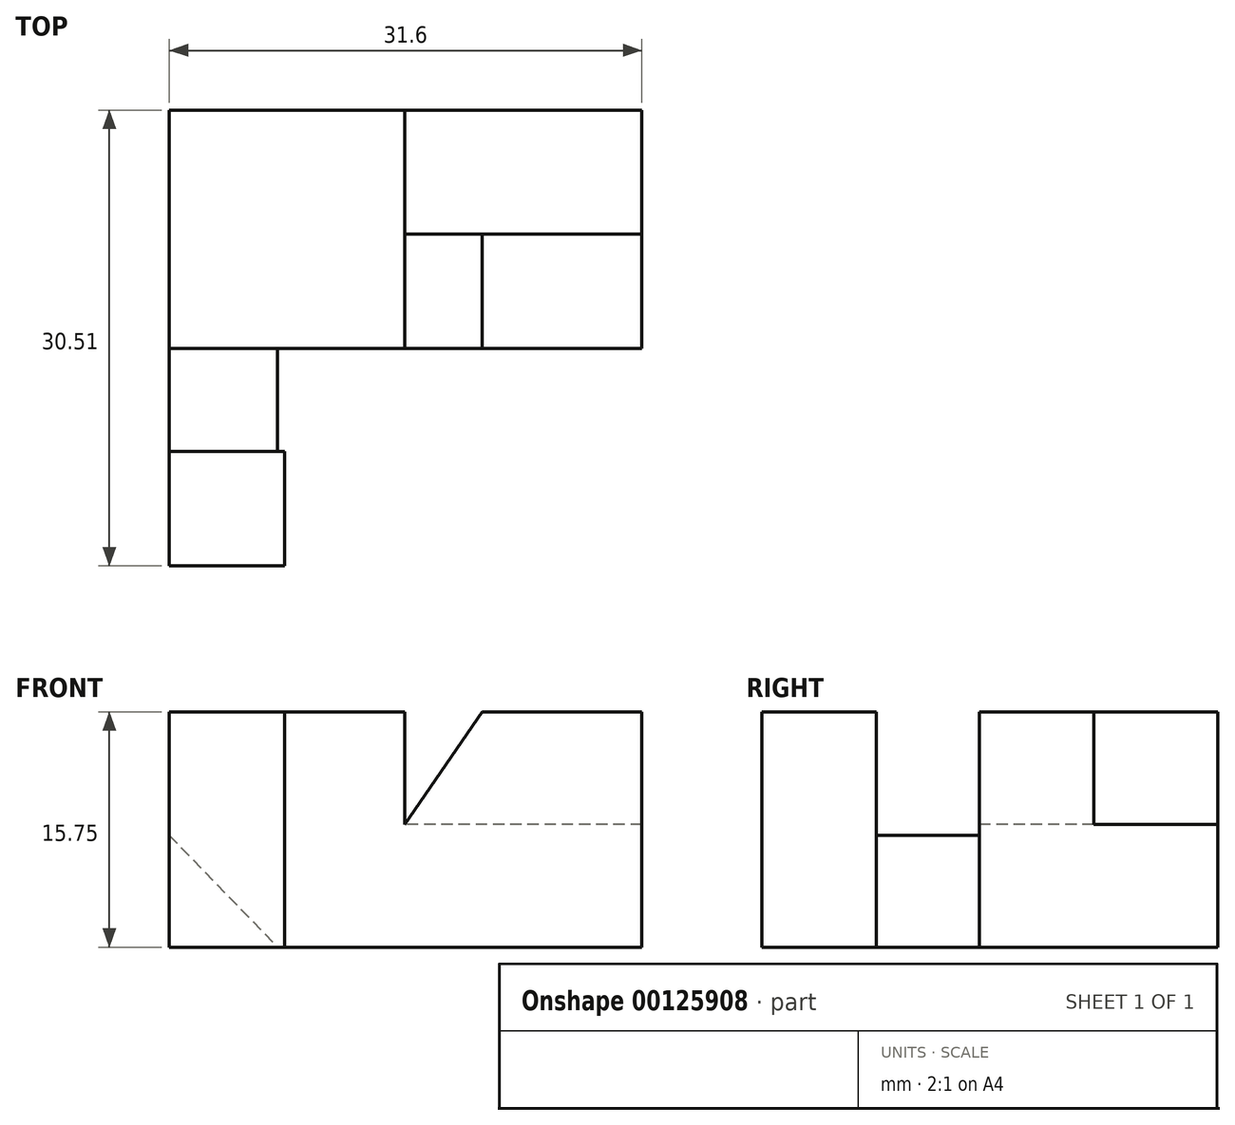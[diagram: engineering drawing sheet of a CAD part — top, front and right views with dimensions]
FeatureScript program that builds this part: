
annotation { "Feature Type Name" : "Feature", "Feature Type Description" : "" }
export const myFeature = defineFeature(function(context is Context, id is Id, definition is map)
    precondition{}
    {
        {
            var Q0;
            Q0=qCreatedBy(makeId("Front.planeOp"),FACE);
            var sketch = newSketch(context, id + "F0", { "sketchPlane" : qUnion([Q0])});
            skLineSegment(sketch, "E0.bottom", {"start": v(0, 0) * mm, "end": v(15.75, 0) * mm});
            skLineSegment(sketch, "E0.top", {"start": v(0, 15.75) * mm, "end": v(15.75, 15.75) * mm});
            skLineSegment(sketch, "E0.left", {"start": v(0, 0) * mm, "end": v(0, 15.75) * mm});
            skLineSegment(sketch, "E0.right", {"start": v(15.75, 0) * mm, "end": v(15.75, 15.75) * mm});
            skSolve(sketch);
        }
        {
            var Q0;
            Q0=makeQuery(id+"F0.imprint","IMPRINT",FACE,{"disambiguationData":[TD([[makeQuery(id+"F0.imprint","IMPRINT",EDGE,{"derivedFrom":sQuery(id+"F0.wireOp",EDGE,"E0.bottom")}),1.0]])]});
            extrude(context, id + "F1", {"entities" : qUnion([Q0]), "depth" : 15.95 * mm});
        }
        {
            var Q0;
            Q0=makeQuery(id+"F1.opExtrude","CAP_FACE",FACE,{"disambiguationData":[OSD([sQuery(id+"F0.wireOp",EDGE,"E0.bottom"),sQuery(id+"F0.wireOp",EDGE,"E0.top"),sQuery(id+"F0.wireOp",EDGE,"E0.left"),sQuery(id+"F0.wireOp",EDGE,"E0.right")])],"isStart":false});
            var sketch = newSketch(context, id + "F2", { "sketchPlane" : qUnion([Q0])});
            skLineSegment(sketch, "E1", {"start": v(0, 0) * mm, "end": v(7.24, 0) * mm});
            skLineSegment(sketch, "E2", {"start": v(0, 0) * mm, "end": v(0, 7.47) * mm});
            skLineSegment(sketch, "E3", {"start": v(0, 7.47) * mm, "end": v(7.24, 0) * mm});
            skSolve(sketch);
        }
        {
            var Q0;
            Q0=makeQuery(id+"F2.imprint","IMPRINT",FACE,{"disambiguationData":[TD([[makeQuery(id+"F2.imprint","IMPRINT",EDGE,{"derivedFrom":sQuery(id+"F2.wireOp",EDGE,"E1")}),1.0]])]});
            extrude(context, id + "F3", {"entities" : qUnion([Q0]), "operationType" : NewBodyOperationType.ADD, "depth" : 6.88 * mm});
        }
        {
            var Q0;
            Q0=makeQuery(id+"F3.opExtrude","CAP_FACE",FACE,{"disambiguationData":[OSD([sQuery(id+"F2.wireOp",EDGE,"E1"),sQuery(id+"F2.wireOp",EDGE,"E2"),sQuery(id+"F2.wireOp",EDGE,"E3")])],"isStart":false});
            var sketch = newSketch(context, id + "F4", { "sketchPlane" : qUnion([Q0])});
            skLineSegment(sketch, "E4", {"start": v(0, 0) * mm, "end": v(7.7, 0) * mm});
            skLineSegment(sketch, "E5", {"start": v(7.7, 0) * mm, "end": v(7.7, 15.75) * mm});
            skLineSegment(sketch, "E6", {"start": v(0, 15.75) * mm, "end": v(0, 0) * mm});
            skLineSegment(sketch, "E7.0", {"start": v(0, 15.75) * mm, "end": v(7.7, 15.75) * mm});
            skPoint(sketch, "E8.end.orphan", {"position": v(0, 16.05) * mm});
            skPoint(sketch, "E9.orphan", {"position": v(7.7, 16.05) * mm});
            skPoint(sketch, "E10.orphan", {"position": v(15.75, 15.75) * mm});
            skSolve(sketch);
        }
        {
            var Q0;
            {var subQ4=sQuery(id+"F4.wireOp",EDGE,"E5");Q0=makeQuery(id+"F4.imprint","IMPRINT",FACE,{"disambiguationData":[TD([[makeQuery(id+"F4.imprint","IMPRINT",EDGE,{"derivedFrom":subQ4}),1.0]])]});}
            var Q1;
            {var subQ3=makeQuery(id+"F3.opExtrude","CAP_EDGE",EDGE,{"disambiguationData":[OSD([sQuery(id+"F2.wireOp",EDGE,"E3")])],"isStart":false});Q1=makeQuery(id+"F4.imprint","IMPRINT",FACE,{"disambiguationData":[TD([[makeQuery(id+"F4.imprint","IMPRINT",EDGE,{"derivedFrom":subQ3}),-1.0]])]});}
            extrude(context, id + "F5", {"entities" : qUnion([Q0, Q1]), "operationType" : NewBodyOperationType.ADD, "depth" : 7.67 * mm});
        }
        {
            var Q0;
            Q0=makeQuery(id+"F1.opExtrude","SWEPT_FACE",FACE,{"disambiguationData":[OSD([sQuery(id+"F0.wireOp",EDGE,"E0.right")])]});
            var sketch = newSketch(context, id + "F6", { "sketchPlane" : qUnion([Q0])});
            skLineSegment(sketch, "E11", {"start": v(0, 0) * mm, "end": v(0, 8.2) * mm});
            skLineSegment(sketch, "E12.bottom", {"start": v(0, 8.2) * mm, "end": v(-15.95, 8.2) * mm});
            skLineSegment(sketch, "E12.top", {"start": v(0, 0) * mm, "end": v(-15.95, 0) * mm});
            skLineSegment(sketch, "E12.left", {"start": v(0, 8.2) * mm, "end": v(0, 0) * mm});
            skLineSegment(sketch, "E12.right", {"start": v(-15.95, 8.2) * mm, "end": v(-15.95, 0) * mm});
            skSolve(sketch);
        }
        {
            var Q0;
            Q0=makeQuery(id+"F6.imprint","IMPRINT",FACE,{"disambiguationData":[TD([[makeQuery(id+"F6.imprint","IMPRINT",EDGE,{"derivedFrom":sQuery(id+"F6.wireOp",EDGE,"E12.bottom")}),1.0]])]});
            extrude(context, id + "F7", {"entities" : qUnion([Q0]), "operationType" : NewBodyOperationType.ADD, "depth" : 15.85 * mm});
        }
        {
            var Q0;
            Q0=makeQuery(id+"F7.boolean.opBoolean","MERGE",FACE,{"derivedFrom":[makeQuery(id+"F1.opExtrude","CAP_FACE",FACE,{"disambiguationData":[OSD([sQuery(id+"F0.wireOp",EDGE,"E0.bottom"),sQuery(id+"F0.wireOp",EDGE,"E0.top"),sQuery(id+"F0.wireOp",EDGE,"E0.left"),sQuery(id+"F0.wireOp",EDGE,"E0.right")])],"isStart":false}),makeQuery(id+"F7.opExtrude","SWEPT_FACE",FACE,{"disambiguationData":[OSD([sQuery(id+"F6.wireOp",EDGE,"E12.right")])]})]});
            var sketch = newSketch(context, id + "F8", { "sketchPlane" : qUnion([Q0])});
            skLineSegment(sketch, "E13", {"start": v(15.75, 8.2) * mm, "end": v(20.92, 15.75) * mm});
            skLineSegment(sketch, "E14", {"start": v(20.92, 15.75) * mm, "end": v(31.6, 15.75) * mm});
            skLineSegment(sketch, "E15", {"start": v(31.6, 15.75) * mm, "end": v(31.6, 8.2) * mm});
            skSolve(sketch);
        }
        {
            var Q0;
            Q0=qSketchRegion(id+"F8",true);
            var Q1;
            Q1=makeQuery(id+"F8.imprint","IMPRINT",FACE,{"disambiguationData":[TD([[makeQuery(id+"F8.imprint","IMPRINT",EDGE,{"derivedFrom":sQuery(id+"F8.wireOp",EDGE,"E13")}),-1.0]])]});
            extrude(context, id + "F9", {"entities" : qUnion([Q0, Q1]), "operationType" : NewBodyOperationType.ADD, "oppositeDirection" : true, "depth" : 7.65 * mm});
        }
    });
